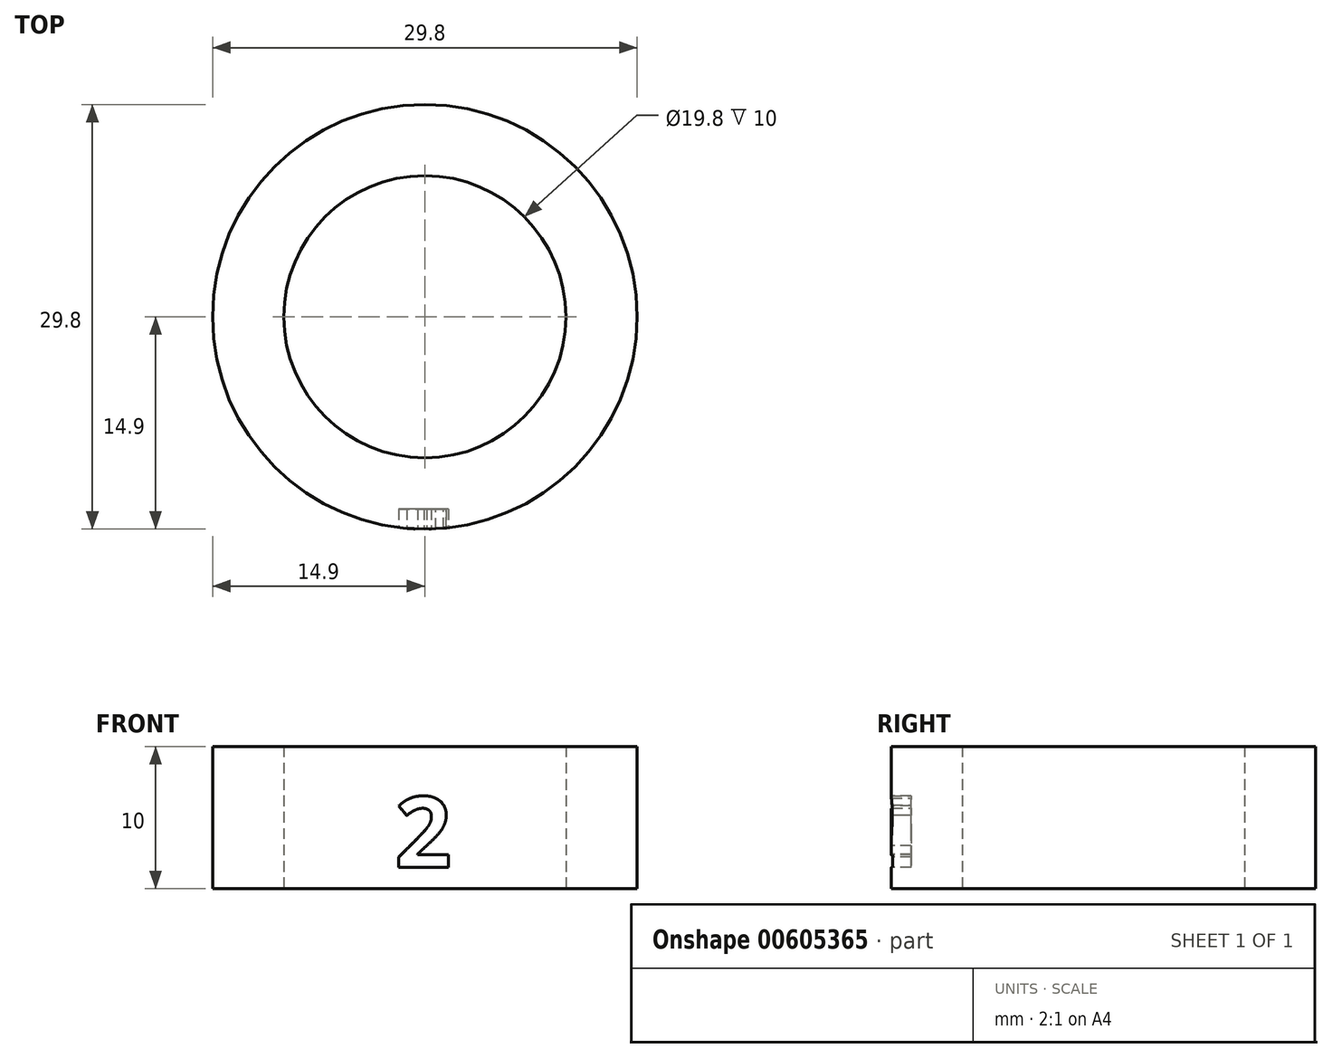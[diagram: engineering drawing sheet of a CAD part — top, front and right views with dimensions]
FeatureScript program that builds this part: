
annotation { "Feature Type Name" : "Feature", "Feature Type Description" : "" }
export const myFeature = defineFeature(function(context is Context, id is Id, definition is map)
    precondition{}
    {
        {
            var Q0;
            Q0=qCreatedBy(makeId("Top.planeOp"),FACE);
            var sketch = newSketch(context, id + "F0", { "sketchPlane" : qUnion([Q0])});
            skCircle(sketch, "E0", {"center": v(0, 0) * mm, "radius": 14.9 * mm});
            skCircle(sketch, "E1", {"center": v(0, 0) * mm, "radius": 15 * mm, "construction": true});
            skCircle(sketch, "E2", {"center": v(0, 0) * mm, "radius": 9.9 * mm});
            skSolve(sketch);
        }
        {
            var Q0;
            Q0=qSketchRegion(id+"F0",true);
            extrude(context, id + "F1", {"entities" : qUnion([Q0]), "depth" : 10 * mm, "offsetDistance" : 25 * mm});
        }
        {
            var Q0;
            Q0=qCreatedBy(makeId("Front.planeOp"),FACE);
            cPlane(context, id + "F2", {"entities" : qUnion([Q0]), "cplaneType" : CPlaneType.OFFSET, "offset" : 15 * mm, "width" : 150 * mm, "height" : 150 * mm});
        }
        {
            var Q0;
            Q0=qCreatedBy(id+"F2.planeOp",FACE);
            var sketch = newSketch(context, id + "F3", { "sketchPlane" : qUnion([Q0])});
            skText(sketch, "E3", { "text": "2", "fontName": "OpenSans-Bold.ttf"});
            const initialGuessF3  = {"E3": [-0.0021, 0.0015, 1, 0, 0.005]};
            skSetInitialGuess(sketch, initialGuessF3);
            skSolve(sketch);
        }
        {
            var Q0;
            Q0=qSketchRegion(id+"F3",true);
            extrude(context, id + "F4", {"entities" : qUnion([Q0]), "operationType" : NewBodyOperationType.REMOVE, "oppositeDirection" : true, "depth" : 1.5 * mm, "offsetDistance" : 25 * mm});
        }
    });
